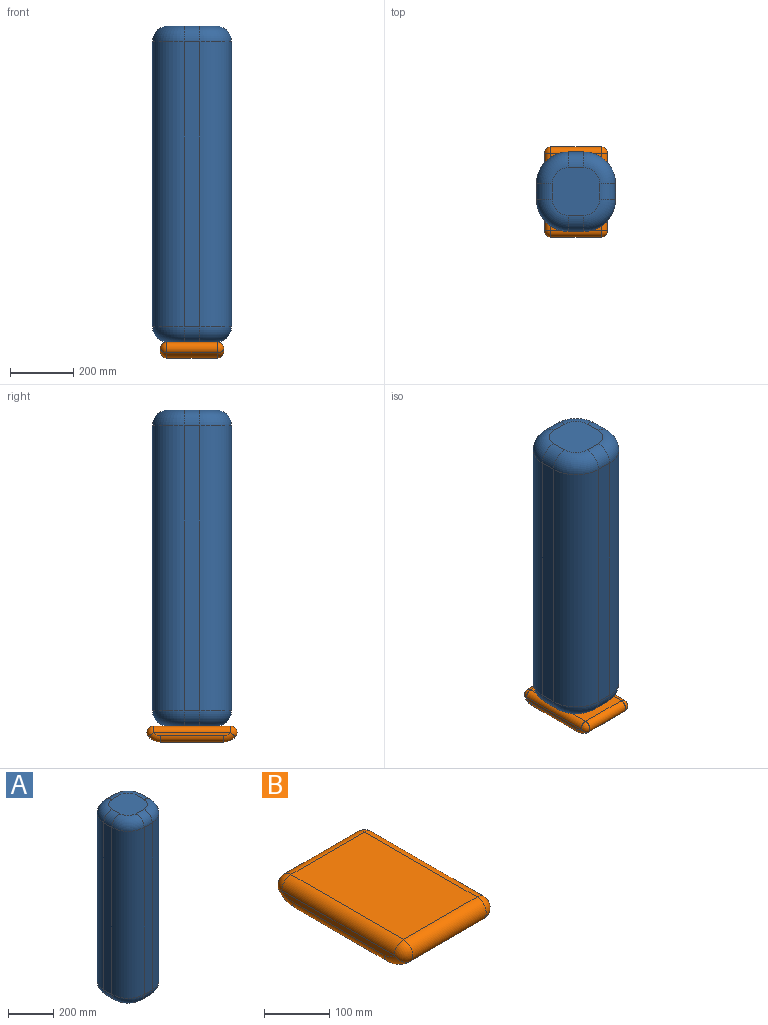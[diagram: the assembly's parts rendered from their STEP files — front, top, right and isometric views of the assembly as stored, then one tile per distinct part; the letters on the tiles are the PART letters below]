
ASSEMBLY  parts=2 mates=1
PART A: 26 faces, bbox 266.5x266.5x1000 mm
  f0: plane 900x50mm, normal (1,0,0), area 45000mm2, adj f6,f9,f15,f24
  f1: plane 900x50mm, normal (0,1,0), area 45000mm2, adj f6,f7,f16,f23
  f2: plane 900x50mm, normal (-1,0,0), area 45000mm2, adj f7,f8,f12,f19
  f3: plane 900x50mm, normal (0,-1,0), area 45000mm2, adj f8,f9,f11,f20
  f4: plane 150x150mm, normal (0,0,1), area 20354mm2, adj f10,f11,f12,f13,f14,f15,f16,f17
  f5: plane 150x150mm, normal (0,0,-1), area 20354mm2, adj f18,f19,f20,f21,f22,f23,f24,f25
  f6: cylinder r=100mm len=900mm, axis (0,0,1), area 141371.7mm2, adj f0,f1,f17,f25
  f7: cylinder r=100mm len=900mm, axis (0,0,-1), area 141371.7mm2, adj f1,f2,f14,f21
  f8: cylinder r=100mm len=900mm, axis (0,0,1), area 141371.7mm2, adj f2,f3,f10,f18
  f9: cylinder r=100mm len=900mm, axis (0,0,-1), area 141371.7mm2, adj f0,f3,f13,f22
  f10: torus R=50mm, axis (0,0,1), area 10095.5mm2, adj f4,f8,f11,f12
  f11: cylinder r=50mm len=50mm, axis (-1,0,0), area 3927mm2, adj f3,f4,f10,f13
  f12: cylinder r=50mm len=50mm, axis (0,1,0), area 3927mm2, adj f2,f4,f10,f14
  f13: torus R=50mm, axis (0,0,1), area 10095.5mm2, adj f4,f9,f11,f15
  f14: torus R=50mm, axis (0,0,1), area 10095.5mm2, adj f4,f7,f12,f16
  f15: cylinder r=50mm len=50mm, axis (0,-1,0), area 3927mm2, adj f0,f4,f13,f17
  f16: cylinder r=50mm len=50mm, axis (1,0,0), area 3927mm2, adj f1,f4,f14,f17
  f17: torus R=50mm, axis (0,0,1), area 10095.5mm2, adj f4,f6,f15,f16
  f18: torus R=50mm, axis (0,0,1), area 10095.5mm2, adj f5,f8,f19,f20
  f19: cylinder r=50mm len=50mm, axis (0,-1,0), area 3927mm2, adj f2,f5,f18,f21
  f20: cylinder r=50mm len=50mm, axis (1,0,0), area 3927mm2, adj f3,f5,f18,f22
  f21: torus R=50mm, axis (0,0,1), area 10095.5mm2, adj f5,f7,f19,f23
  f22: torus R=50mm, axis (0,0,1), area 10095.5mm2, adj f5,f9,f20,f24
  f23: cylinder r=50mm len=50mm, axis (-1,0,0), area 3927mm2, adj f1,f5,f21,f25
  f24: cylinder r=50mm len=50mm, axis (0,1,0), area 3927mm2, adj f0,f5,f22,f25
  f25: torus R=50mm, axis (0,0,1), area 10095.5mm2, adj f5,f6,f23,f24
PART B: 20 faces, bbox 200x284.7x54.1 mm
  f0: plane 244.72x10mm, normal (1,0,0), area 2309.7mm2, adj f14,f15,f17,f19
  f1: plane 244.72x10mm, normal (-1,0,0), area 2309.7mm2, adj f6,f8,f10,f11
  f2: plane 244.72x160mm, normal (0,0,1), area 39155.4mm2, adj f9,f10,f15,f16
  f3: plane 200x160mm, normal (0,0,-1), area 32000mm2, adj f4,f5,f8,f17
  f4: cylinder r=50mm len=160mm, axis (-1,0,0), area 6728.5mm2, adj f3,f11,f16,f19
  f5: cylinder r=50mm len=160mm, axis (1,0,0), area 6728.5mm2, adj f3,f6,f9,f14
  f6: torus R=30mm, axis (1,0,0), area 1129.1mm2, adj f1,f5,f7,f8
  f7: sphere r=20mm, area 920.2mm2, adj f6,f9,f10
  f8: cylinder r=20mm len=200mm, axis (0,-1,0), area 6283.2mm2, adj f1,f3,f6,f11
  f9: cylinder r=20mm len=160mm, axis (1,0,0), area 7361.7mm2, adj f2,f5,f7,f12
  f10: cylinder r=20mm len=244.72mm, axis (0,1,0), area 7688.1mm2, adj f1,f2,f7,f13
  f11: torus R=30mm, axis (1,0,0), area 1129.1mm2, adj f1,f4,f8,f13
  f12: sphere r=20mm, area 920.2mm2, adj f9,f14,f15
  f13: sphere r=20mm, area 920.2mm2, adj f10,f11,f16
  f14: torus R=30mm, axis (1,0,0), area 1129.1mm2, adj f0,f5,f12,f17
  f15: cylinder r=20mm len=244.72mm, axis (0,-1,0), area 7688.1mm2, adj f0,f2,f12,f18
  f16: cylinder r=20mm len=160mm, axis (-1,0,0), area 7361.7mm2, adj f2,f4,f13,f18
  f17: cylinder r=20mm len=200mm, axis (0,1,0), area 6283.2mm2, adj f0,f3,f14,f19
  f18: sphere r=20mm, area 920.2mm2, adj f15,f16,f19
  f19: torus R=30mm, axis (1,0,0), area 1129.1mm2, adj f0,f4,f17,f18
PLACE A t=(-218.25,-111.87,46.2)mm
PLACE B t=(-218.25,-111.87,21.2)mm
MATE fastened A.f5 <-> B.f2  axis (0,0,-1) through (-218.25,-111.87,46.2)mm
